# Revit family: Supercal 5_RFA
name_source: partatom
category: Data Devices
units: mm (PartAtom-declared; Revit-internal decimal feet)

## family parameters
Cut with Voids When Loaded = No
Host = Face
Maintain Annotation Orientation = No
Part Type = Normal
Room Calculation Point = No
Round Connector Dimension = Use Diameter
Shared = No

## types (10) — shared parameters
Body Material = Danfoss Plastic White
Default Elevation = 1219.2 mm  [stored 4 ft]
Description = Energy Calculator
H = 61 mm  [stored 0.200131 ft]
H1 = 7.6 mm
H2 = 3.62 mm  [stored 0.0118766 ft]
H3 = 44.4 mm  [stored 0.145669 ft]
IfcExportAs = IfcValveType
IfcExportType = Supercal 5
Interface Module = No interface module
Intergrated Communication = M-Bus
L = 143 mm
L1 = 4.3 mm
L2 = 5 mm  [stored 0.0164042 ft]
L3 = 5.1 mm  [stored 0.0167323 ft]
L4 = 27.3 mm
L5 = 18.5 mm  [stored 0.0606955 ft]
LB1 = 124.4 mm  [stored 0.408136 ft]
LB2 = 136.96 mm  [stored 0.449344 ft]
LB3 = 12 mm  [stored 0.0393701 ft]
LB4 = 35 mm  [stored 0.114829 ft]
LB5 = 70 mm  [stored 0.229659 ft]
LOD 200 = No
LOD 350 = Yes
Manufacturer = Danfoss
Max Medium Temperature = 55 °C
Min Medium Temperature = 5 °C
URL = https://store.danfoss.com
W = 158 mm  [stored 0.518373 ft]
WB1 = 56.2 mm  [stored 0.184383 ft]
WB2 = 48.55 mm  [stored 0.159285 ft]
WB3 = 28.7 mm  [stored 0.0941601 ft]
WB4 = 12 mm  [stored 0.0393701 ft]

## per-type parameters (varying)
| type | Energy Unit | Installation | Max Diameter | Max Flow | Max Flow (Text) | Min Diameter | Min Flow | Model | Model Type | Pulse Value Volume | Supply Voltage Type | Voltage | Weight |
| Supercal 5_2.5l/p_3.6V_M-Bus_187F8300 | 0.01 MWh | Supply | 150 mm | 300.0 m³/h | 300 m³/h | 100 mm  [stored 0.328084 ft] | 60 m³/h | 187F8300 | Supercal 5_2.5l/p_3.6V_M-Bus | 2.5 l/pulse | battery D-cell | 4 V | 0.69 kg |
| Supercal 5_10l/p_3.6V_M-Bus_187F8301 | 0.01 MWh | Supply | 350 mm  [stored 1.14829 ft] | 1500.0 m³/h | 1500 m³/h | 200 mm  [stored 0.656168 ft] | 250 m³/h | 187F8301 | Supercal 5_10l/p_3.6V_M-Bus | 10 l/pulse | battery D-cell | 4 V | 0.69 kg |
| Supercal 5_50/p_3.6V_M-Bus_187F8302 | 0.01 MWh | Supply | 500 mm  [stored 1.64042 ft] | 2950.0 m³/h | 2950 m³/h | 400 mm  [stored 1.31234 ft] | 950 m³/h | 187F8302 | Supercal 5_50l/p_3.6V_M-Bus | 50 l/pulse | battery D-cell | 4 V | 0.69 kg |
| Supercal 5_100l/p_3.6V_M-Bus_187F8303 | 0.01 MWh | Supply | 1200 mm | 10000.0 m³/h | 10000 m³/h | 600 mm | 2150 m³/h | 187F8303 | Supercal 5_100l/p_3.6V_M-Bus | 100 l/pulse | battery D-cell | 4 V | 0.69 kg |
| Supercal 5_1l/p_3.6V_M-Bus_187F8304 | 1 kWh | Supply | 1200 mm | 25.0 m³/h | 25 m³/h | 600 mm | 6 m³/h | 187F8304 | Supercal 5_1l/p_3.6V_M-Bus | 1 l/pulse | battery D-cell | 4 V | 0.69 kg |
| Supercal 5_2.5l/p_230V_M-Bus_187F8305 | 0.01 MWh | Return | 1200 mm | 300.0 m³/h | 300 m³/h | 600 mm | 60 m³/h | 187F8305 | Supercal 5_2.5l/p_230V_M-Bus | 2.5 l/pulse | mains unit | 230 V | 0.63 kg |
| Supercal 5_10l/p_230V_M-Bus_187F8306 | 0.01 MWh | Return | 1200 mm | 1500.0 m³/h | 1500 m³/h | 600 mm | 250 m³/h | 187F8306 | Supercal 5_10l/p_230V_M-Bus | 10 l/pulse | mains unit | 230 V | 0.63 kg |
| Supercal 5_50l/p_230V_M-Bus_187F8307 | 0.01 MWh | Return | 1200 mm | 2950.0 m³/h | 2950 m³/h | 600 mm | 950 m³/h | 187F8307 | Supercal 5_50l/p_230V_M-Bus | 50 l/pulse | mains unit | 230 V | 0.63 kg |
| Supercal 5_100l/p_230V_M-Bus_187F8308 | 0.01 MWh | Return | 1200 mm | 10000.0 m³/h | 10000 m³/h | 600 mm | 2150 m³/h | 187F8308 | Supercal 5_100l/p_230V_M-Bus | 100 l/pulse | mains unit | 230 V | 0.63 kg |
| Supercal 5_1l/p_230V_M-Bus_187F8309 | 1 kWh | Return | 1200 mm | 25.0 m³/h | 25 m³/h | 600 mm | 6 m³/h | 187F8309 | Supercal 5_1l/p_230V_M-Bus | 1 l/pulse | mains unit | 230 V | 0.63 kg |

note: [stored X ft] marks values corroborated as IEEE doubles in the binary element streams (Revit-internal decimal feet)

## geometry (parser evidence)
native form markers: Sweep x1
no freeform markers — native parametric forms only
